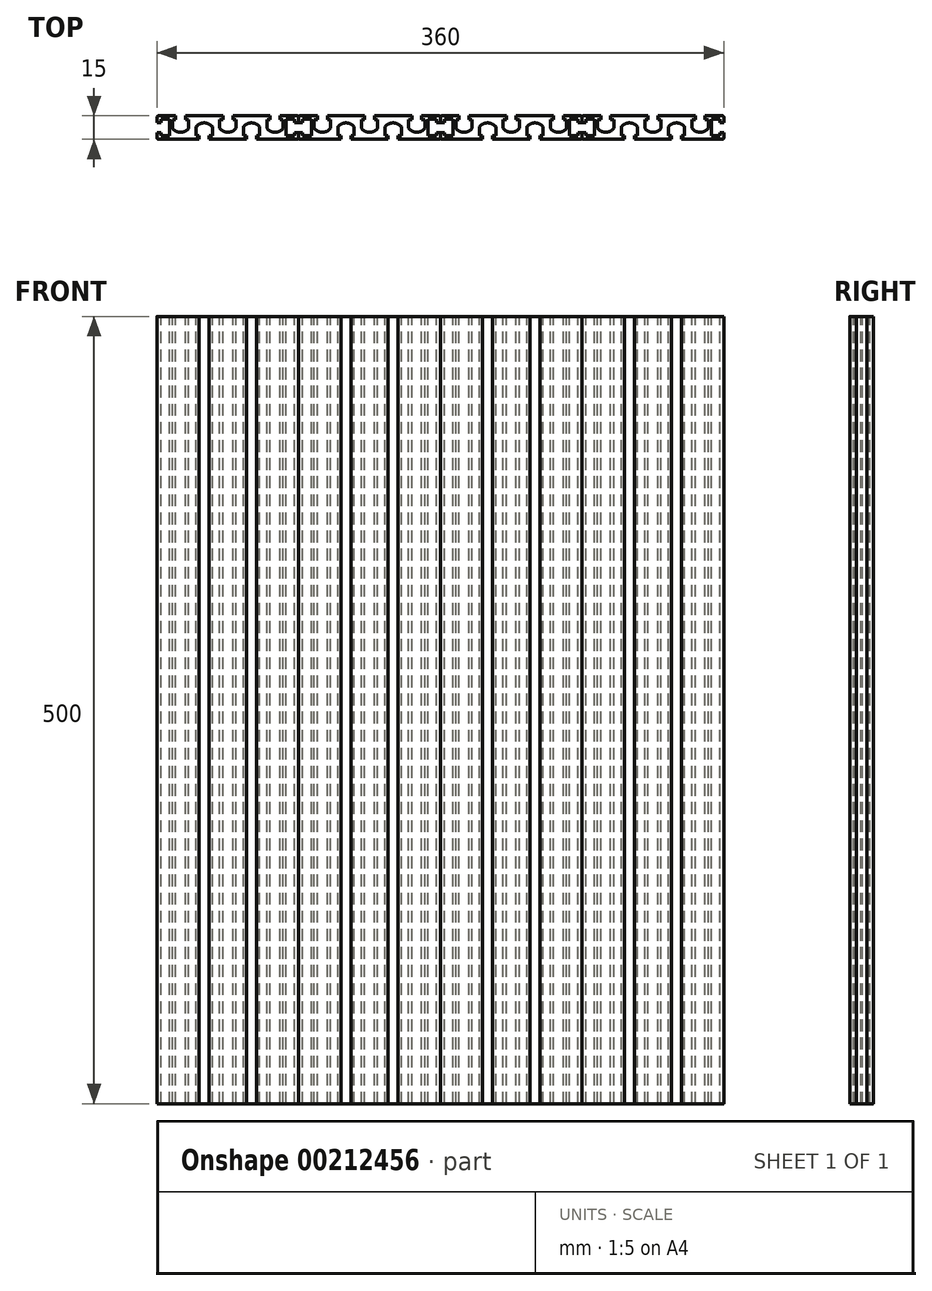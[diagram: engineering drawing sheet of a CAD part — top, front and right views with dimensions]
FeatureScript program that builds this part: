
annotation { "Feature Type Name" : "Feature", "Feature Type Description" : "" }
export const myFeature = defineFeature(function(context is Context, id is Id, definition is map)
    precondition{}
    {
        {
            var Q0;
            Q0=qCreatedBy(makeId("Top.planeOp"),FACE);
            var sketch = newSketch(context, id + "F0", { "sketchPlane" : qUnion([Q0])});
            skLineSegment(sketch, "E0.bottom", {"start": v(45, 7.5) * mm, "end": v(-45, 7.5) * mm});
            skLineSegment(sketch, "E0.top", {"start": v(45, -7.5) * mm, "end": v(-45, -7.5) * mm});
            skLineSegment(sketch, "E0.left", {"start": v(45, 7.5) * mm, "end": v(45, -7.5) * mm});
            skLineSegment(sketch, "E0.right", {"start": v(-45, 7.5) * mm, "end": v(-45, -7.5) * mm});
            skPoint(sketch, "E0.middle", {"position": v(0, 0) * mm});
            skSolve(sketch);
        }
        {
            assignVariable(context, id + "F1", {"name" : "L", "anyValue" : 500});
        }
        {
            var Q0;
            Q0=qSketchRegion(id+"F0",true);
            extrude(context, id + "F2", {"entities" : qUnion([Q0]), "endBound" : BoundingType.SYMMETRIC, "depth" : (getVariable(context, 'L')) * mm});
        }
        {
            var Q0;
            Q0=qCreatedBy(makeId("Top.planeOp"),FACE);
            var sketch = newSketch(context, id + "F3", { "sketchPlane" : qUnion([Q0])});
            skLineSegment(sketch, "E1", {"start": v(-3.15, 7.5) * mm, "end": v(3.15, 7.5) * mm});
            skLineSegment(sketch, "E2", {"start": v(3.15, 7.5) * mm, "end": v(3.15, 5) * mm});
            skLineSegment(sketch, "E3", {"start": v(3.15, 5) * mm, "end": v(5.15, 5) * mm});
            skLineSegment(sketch, "E4", {"start": v(5.15, 5) * mm, "end": v(5.15, -0.5) * mm});
            skLineSegment(sketch, "E5", {"start": v(-3.15, 7.5) * mm, "end": v(-3.15, 5) * mm});
            skLineSegment(sketch, "E6", {"start": v(-3.15, 5) * mm, "end": v(-5.15, 5) * mm});
            skLineSegment(sketch, "E7", {"start": v(-5.15, 5) * mm, "end": v(-5.15, -0.5) * mm});
            skArc(sketch, "E8", {"start": v(-5.15, -0.5) * mm, "mid": v(0, -3) * mm, "end": v(5.15, -0.5) * mm});
            skLineSegment(sketch, "E9", {"start": v(0, 7.5) * mm, "end": v(0, 3.55) * mm, "construction": true});
            skLineSegment(sketch, "E10.1.0.0", {"start": v(35.15, 5) * mm, "end": v(35.15, -0.5) * mm});
            skLineSegment(sketch, "E10.1.0.1", {"start": v(24.85, 5) * mm, "end": v(24.85, -0.5) * mm});
            skLineSegment(sketch, "E10.1.0.2", {"start": v(26.85, 7.5) * mm, "end": v(26.85, 5) * mm});
            skArc(sketch, "E10.1.0.3", {"start": v(24.85, -0.5) * mm, "mid": v(30, -3) * mm, "end": v(35.15, -0.5) * mm});
            skLineSegment(sketch, "E10.1.0.4", {"start": v(30, 7.5) * mm, "end": v(30, 3.55) * mm, "construction": true});
            skLineSegment(sketch, "E10.1.0.5", {"start": v(33.15, 7.5) * mm, "end": v(33.15, 5) * mm});
            skLineSegment(sketch, "E10.1.0.6", {"start": v(26.85, 7.5) * mm, "end": v(33.15, 7.5) * mm});
            skLineSegment(sketch, "E10.1.0.7", {"start": v(26.85, 5) * mm, "end": v(24.85, 5) * mm});
            skLineSegment(sketch, "E10.1.0.8", {"start": v(33.15, 5) * mm, "end": v(35.15, 5) * mm});
            skLineSegment(sketch, "E10.direction1", {"start": v(-5.15, -0.5) * mm, "end": v(24.85, -0.5) * mm, "construction": true});
            skArc(sketch, "E11.1.0.0", {"start": v(-35.15, -0.5) * mm, "mid": v(-30, -3) * mm, "end": v(-24.85, -0.5) * mm});
            skLineSegment(sketch, "E11.1.0.1", {"start": v(-35.15, 5) * mm, "end": v(-35.15, -0.5) * mm});
            skLineSegment(sketch, "E11.1.0.2", {"start": v(-33.15, 5) * mm, "end": v(-35.15, 5) * mm});
            skLineSegment(sketch, "E11.1.0.3", {"start": v(-33.15, 7.5) * mm, "end": v(-33.15, 5) * mm});
            skLineSegment(sketch, "E11.1.0.4", {"start": v(-30, 7.5) * mm, "end": v(-30, 3.55) * mm, "construction": true});
            skLineSegment(sketch, "E11.1.0.5", {"start": v(-24.85, 5) * mm, "end": v(-24.85, -0.5) * mm});
            skLineSegment(sketch, "E11.1.0.6", {"start": v(-26.85, 7.5) * mm, "end": v(-26.85, 5) * mm});
            skLineSegment(sketch, "E11.1.0.7", {"start": v(-33.15, 7.5) * mm, "end": v(-26.85, 7.5) * mm});
            skLineSegment(sketch, "E11.1.0.8", {"start": v(-26.85, 5) * mm, "end": v(-24.85, 5) * mm});
            skLineSegment(sketch, "E11.direction1", {"start": v(-5.15, -0.5) * mm, "end": v(-35.15, -0.5) * mm, "construction": true});
            skLineSegment(sketch, "E12", {"start": v(-18.15, -7.5) * mm, "end": v(-11.85, -7.5) * mm});
            skLineSegment(sketch, "E13", {"start": v(-11.85, -7.5) * mm, "end": v(-11.85, -5) * mm});
            skLineSegment(sketch, "E14", {"start": v(-11.85, -5) * mm, "end": v(-9.85, -5) * mm});
            skLineSegment(sketch, "E15", {"start": v(-9.85, -5) * mm, "end": v(-9.85, 0.5) * mm});
            skLineSegment(sketch, "E16", {"start": v(-18.15, -7.5) * mm, "end": v(-18.15, -5) * mm});
            skLineSegment(sketch, "E17", {"start": v(-18.15, -5) * mm, "end": v(-20.15, -5) * mm});
            skLineSegment(sketch, "E18", {"start": v(-20.15, -5) * mm, "end": v(-20.15, 0.5) * mm});
            skArc(sketch, "E19", {"start": v(-9.85, 0.5) * mm, "mid": v(-15, 3) * mm, "end": v(-20.15, 0.5) * mm});
            skLineSegment(sketch, "E20", {"start": v(-15, -7.5) * mm, "end": v(-15, 3) * mm, "construction": true});
            skArc(sketch, "E21.1.0.0", {"start": v(20.15, 0.5) * mm, "mid": v(15, 3) * mm, "end": v(9.85, 0.5) * mm});
            skLineSegment(sketch, "E21.1.0.1", {"start": v(20.15, -5) * mm, "end": v(20.15, 0.5) * mm});
            skLineSegment(sketch, "E21.1.0.2", {"start": v(18.15, -5) * mm, "end": v(20.15, -5) * mm});
            skLineSegment(sketch, "E21.1.0.3", {"start": v(9.85, -5) * mm, "end": v(9.85, 0.5) * mm});
            skLineSegment(sketch, "E21.1.0.4", {"start": v(18.15, -7.5) * mm, "end": v(18.15, -5) * mm});
            skLineSegment(sketch, "E21.1.0.5", {"start": v(15, -7.5) * mm, "end": v(15, 3) * mm, "construction": true});
            skLineSegment(sketch, "E21.1.0.6", {"start": v(11.85, -5) * mm, "end": v(9.85, -5) * mm});
            skLineSegment(sketch, "E21.1.0.7", {"start": v(11.85, -7.5) * mm, "end": v(18.15, -7.5) * mm});
            skLineSegment(sketch, "E21.1.0.8", {"start": v(11.85, -7.5) * mm, "end": v(11.85, -5) * mm});
            skLineSegment(sketch, "E21.direction1", {"start": v(-18.15, -7.5) * mm, "end": v(11.85, -7.5) * mm, "construction": true});
            skLineSegment(sketch, "E22", {"start": v(-45, 3.25) * mm, "end": v(-45, -3.25) * mm});
            skLineSegment(sketch, "E23", {"start": v(-45, -3.25) * mm, "end": v(-42.5, -3.25) * mm});
            skLineSegment(sketch, "E24", {"start": v(-42.5, -3.25) * mm, "end": v(-42.5, -5.25) * mm});
            skLineSegment(sketch, "E25", {"start": v(-42.5, -5.25) * mm, "end": v(-37, -5.25) * mm});
            skLineSegment(sketch, "E26", {"start": v(-37, -5.25) * mm, "end": v(-37, 5.25) * mm});
            skLineSegment(sketch, "E27", {"start": v(-37, 5.25) * mm, "end": v(-42.5, 5.25) * mm});
            skLineSegment(sketch, "E28", {"start": v(-42.5, 5.25) * mm, "end": v(-42.5, 3.25) * mm});
            skLineSegment(sketch, "E29", {"start": v(-42.5, 3.25) * mm, "end": v(-45, 3.25) * mm});
            skLineSegment(sketch, "E30.MirrorCS", {"start": v(45, -3.25) * mm, "end": v(42.5, -3.25) * mm});
            skLineSegment(sketch, "E31.MirrorCS", {"start": v(42.5, 3.25) * mm, "end": v(45, 3.25) * mm});
            skLineSegment(sketch, "E32.MirrorCS", {"start": v(42.5, -3.25) * mm, "end": v(42.5, -5.25) * mm});
            skLineSegment(sketch, "E33.MirrorCS", {"start": v(45, 3.25) * mm, "end": v(45, -3.25) * mm});
            skLineSegment(sketch, "E34.MirrorCS", {"start": v(37, -5.25) * mm, "end": v(37, 5.25) * mm});
            skLineSegment(sketch, "E35.MirrorCS", {"start": v(42.5, 5.25) * mm, "end": v(42.5, 3.25) * mm});
            skLineSegment(sketch, "E36.MirrorCS", {"start": v(42.5, -5.25) * mm, "end": v(37, -5.25) * mm});
            skLineSegment(sketch, "E37.MirrorCS", {"start": v(37, 5.25) * mm, "end": v(42.5, 5.25) * mm});
            skSolve(sketch);
        }
        {
            var Q0;
            Q0=qSketchRegion(id+"F3",true);
            extrude(context, id + "F4", {"entities" : qUnion([Q0]), "operationType" : NewBodyOperationType.REMOVE, "endBound" : BoundingType.SYMMETRIC, "oppositeDirection" : true, "depth" : (getVariable(context, 'L')) * mm});
        }
        {
            var Q0;
            Q0=makeQuery(id+"F2.opExtrude","SWEPT_EDGE",EDGE,{"disambiguationData":[OSD([sQuery(id+"F0.wireOp",EDGE,"E0.bottom"),sQuery(id+"F0.wireOp",EDGE,"E0.left")])]});
            var Q1;
            Q1=makeQuery(id+"F2.opExtrude","SWEPT_EDGE",EDGE,{"disambiguationData":[OSD([sQuery(id+"F0.wireOp",EDGE,"E0.top"),sQuery(id+"F0.wireOp",EDGE,"E0.left")])]});
            var Q2;
            Q2=makeQuery(id+"F2.opExtrude","SWEPT_EDGE",EDGE,{"disambiguationData":[OSD([sQuery(id+"F0.wireOp",EDGE,"E0.bottom"),sQuery(id+"F0.wireOp",EDGE,"E0.right")])]});
            var Q3;
            Q3=makeQuery(id+"F2.opExtrude","SWEPT_EDGE",EDGE,{"disambiguationData":[OSD([sQuery(id+"F0.wireOp",EDGE,"E0.top"),sQuery(id+"F0.wireOp",EDGE,"E0.right")])]});
            fillet(context, id + "F5", {"entities" : qUnion([Q0, Q1, Q2, Q3]), "radius" : 1 * mm, "tangentPropagation" : true, "allowEdgeOverflow" : false});
        }
        {
            var Q0;
            Q0=makeQuery(id+"F2.opExtrude","SWEPT_BODY",BODY,{"disambiguationData":[OSD([sQuery(id+"F0.wireOp",EDGE,"E0.bottom"),sQuery(id+"F0.wireOp",EDGE,"E0.top"),sQuery(id+"F0.wireOp",EDGE,"E0.left"),sQuery(id+"F0.wireOp",EDGE,"E0.right")])]});
            transform(context, id + "F6", {"entities" : qUnion([Q0]), "transformType" : TransformType.TRANSLATION_3D, "dx" : 90 * mm, "dy" : 0 * mm, "dz" : 0 * mm, "makeCopy" : true});
        }
        {
            var Q0;
            Q0=makeQuery(id+"F6.opPattern","COPY",BODY,{"derivedFrom":makeQuery(id+"F2.opExtrude","SWEPT_BODY",BODY,{"disambiguationData":[OSD([sQuery(id+"F0.wireOp",EDGE,"E0.bottom"),sQuery(id+"F0.wireOp",EDGE,"E0.top"),sQuery(id+"F0.wireOp",EDGE,"E0.left"),sQuery(id+"F0.wireOp",EDGE,"E0.right")])]}),"instanceName":"1"});
            transform(context, id + "F7", {"entities" : qUnion([Q0]), "transformType" : TransformType.TRANSLATION_3D, "dx" : 90 * mm, "dy" : 0 * mm, "dz" : 0 * mm, "makeCopy" : true});
        }
        {
            var Q0;
            Q0=makeQuery(id+"F7.opPattern","COPY",BODY,{"derivedFrom":makeQuery(id+"F6.opPattern","COPY",BODY,{"derivedFrom":makeQuery(id+"F2.opExtrude","SWEPT_BODY",BODY,{"disambiguationData":[OSD([sQuery(id+"F0.wireOp",EDGE,"E0.bottom"),sQuery(id+"F0.wireOp",EDGE,"E0.top"),sQuery(id+"F0.wireOp",EDGE,"E0.left"),sQuery(id+"F0.wireOp",EDGE,"E0.right")])]}),"instanceName":"1"}),"instanceName":"1"});
            transform(context, id + "F8", {"entities" : qUnion([Q0]), "transformType" : TransformType.TRANSLATION_3D, "dx" : 90 * mm, "dy" : 0 * mm, "dz" : 0 * mm, "makeCopy" : true});
        }
    });
